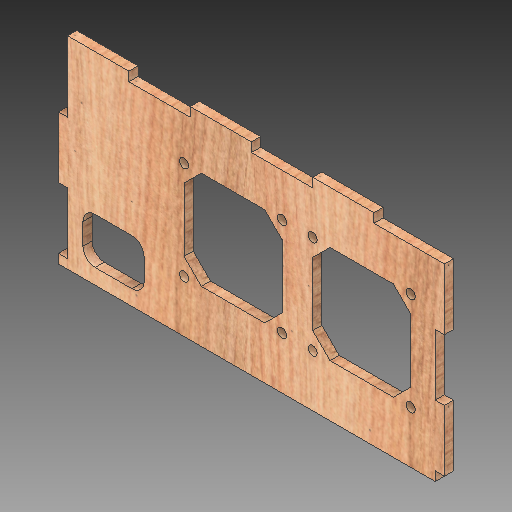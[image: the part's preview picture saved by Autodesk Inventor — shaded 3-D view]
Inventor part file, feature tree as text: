
AUTODESK INVENTOR PART (.ipt)
format: ipt  version: 2018.2 (Build 222227000, 227)  size: 384,000 bytes
history: native  units: mm
features: extrude x3, sketch x3, pattern_linear x1, fillet x1
ambient origin geometry x8: Origin, YZ Plane, XZ Plane, XY Plane, X Axis, Y Axis, Z Axis, Center Point
bodies: Solid1 (feature_tree)
feature tree (8):
  extrude  "Extrusion1"  Depth=120.0mm
  extrude  "Extrusion2"  Depth=20.0mm
  pattern_linear  "Rectangular Pattern1"  Count1=2  [1 undecoded]
  extrude  "Extrusion3"  Depth=3.0mm
  fillet  "Fillet1"  Radius=20.0mm
  sketch  "Sketch1"  dims[d0=3.0mm d1=120.0mm]
  sketch  "Sketch2"  dims[d2=3.0mm d3=20.0mm d4=20.0mm]
  sketch  "Sketch3"  dims[d5=20.0mm d6=3.0mm d7=20.0mm d8=20.0mm d9=20.0mm d10=20.0mm d11=20.0mm d12=20.0mm d13=3.0mm d14=20.0mm d15=20.0mm d16=20.0mm d17=3.0mm d18=0.0mm d19=32.0mm d20=32.0mm d21=8.0mm d26=3.0mm d27=45.0deg d28=4.0mm d29=3.0mm d30=0.0mm d31=20.0mm d33=42.0mm d34=15.0mm d35=5.0mm d36=5.0mm d37=20.0mm d38=10.0mm d39=0.0mm d40=4.0mm]
note: 1 required parameter value undecoded (feature->parameter linkage not recoverable at this tier; creation-order binding heuristic only, values carry confidence <= 0.55)
